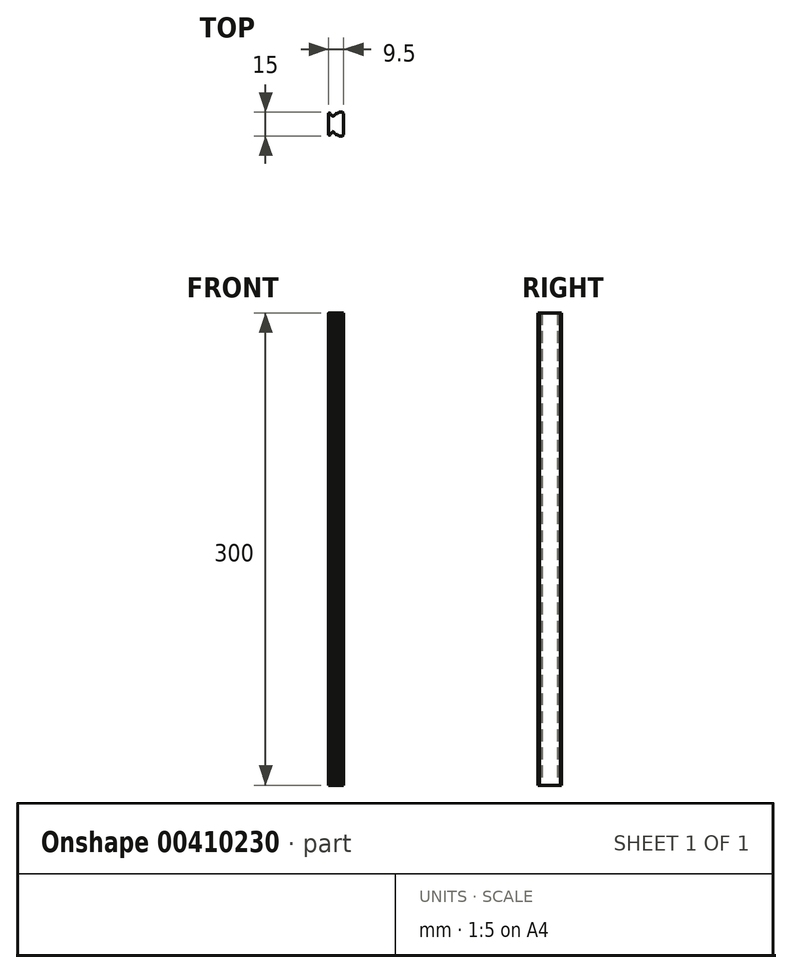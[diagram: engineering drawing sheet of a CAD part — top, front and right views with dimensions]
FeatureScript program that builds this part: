
annotation { "Feature Type Name" : "Feature", "Feature Type Description" : "" }
export const myFeature = defineFeature(function(context is Context, id is Id, definition is map)
    precondition{}
    {
        {
            var Q0;
            Q0=qCreatedBy(makeId("Top.planeOp"),FACE);
            var sketch = newSketch(context, id + "F0", { "sketchPlane" : qUnion([Q0])});
            skLineSegment(sketch, "E0.0.0", {"start": v(-25.68, 29.9) * mm, "end": v(-26.44, 30.34) * mm});
            skArc(sketch, "E0.0.1", {"start": v(-26.44, 30.34) * mm, "mid": v(-26.74, 30.34) * mm, "end": v(-26.89, 30.08) * mm});
            skLineSegment(sketch, "E0.0.2", {"start": v(-26.89, 30.08) * mm, "end": v(-26.89, 16.68) * mm});
            skArc(sketch, "E0.0.3", {"start": v(-26.89, 16.68) * mm, "mid": v(-26.74, 16.42) * mm, "end": v(-26.44, 16.42) * mm});
            skLineSegment(sketch, "E0.0.4", {"start": v(-26.44, 16.42) * mm, "end": v(-25.68, 16.86) * mm});
            skArc(sketch, "E0.0.5", {"start": v(-25.68, 16.86) * mm, "mid": v(-25.27, 17.55) * mm, "end": v(-24.58, 17.97) * mm});
            skArc(sketch, "E0.0.6", {"start": v(-24.58, 17.97) * mm, "mid": v(-24.14, 18.48) * mm, "end": v(-23.7, 17.97) * mm});
            skArc(sketch, "E0.0.7", {"start": v(-23.7, 17.97) * mm, "mid": v(-22.95, 17.5) * mm, "end": v(-22.57, 16.73) * mm});
            skLineSegment(sketch, "E0.0.8", {"start": v(-22.57, 16.73) * mm, "end": v(-21.24, 16.73) * mm});
            skLineSegment(sketch, "E0.0.9", {"start": v(-21.24, 16.73) * mm, "end": v(-20.39, 15.88) * mm});
            skLineSegment(sketch, "E0.0.10", {"start": v(-20.39, 15.88) * mm, "end": v(-18.19, 15.88) * mm});
            skLineSegment(sketch, "E0.0.11", {"start": v(-18.19, 15.88) * mm, "end": v(-17.39, 16.68) * mm});
            skLineSegment(sketch, "E0.0.12", {"start": v(-17.39, 16.68) * mm, "end": v(-17.39, 30.08) * mm});
            skLineSegment(sketch, "E0.0.13", {"start": v(-17.39, 30.08) * mm, "end": v(-18.19, 30.88) * mm});
            skLineSegment(sketch, "E0.0.14", {"start": v(-18.19, 30.88) * mm, "end": v(-20.39, 30.88) * mm});
            skLineSegment(sketch, "E0.0.15", {"start": v(-20.39, 30.88) * mm, "end": v(-21.24, 30.03) * mm});
            skLineSegment(sketch, "E0.0.16", {"start": v(-21.24, 30.03) * mm, "end": v(-22.57, 30.03) * mm});
            skArc(sketch, "E0.0.17", {"start": v(-22.57, 30.03) * mm, "mid": v(-22.95, 29.25) * mm, "end": v(-23.7, 28.8) * mm});
            skArc(sketch, "E0.0.18", {"start": v(-23.7, 28.8) * mm, "mid": v(-24.14, 28.28) * mm, "end": v(-24.58, 28.8) * mm});
            skArc(sketch, "E0.0.19", {"start": v(-24.58, 28.8) * mm, "mid": v(-25.27, 29.2) * mm, "end": v(-25.68, 29.9) * mm});
            skSolve(sketch);
        }
        {
            var Q0;
            Q0 = qSketchRegion(id + "F0", true);
            extrude(context, id + "F1", {"entities" : qUnion([Q0]), "depth" : 300 * mm});
        }
    });
